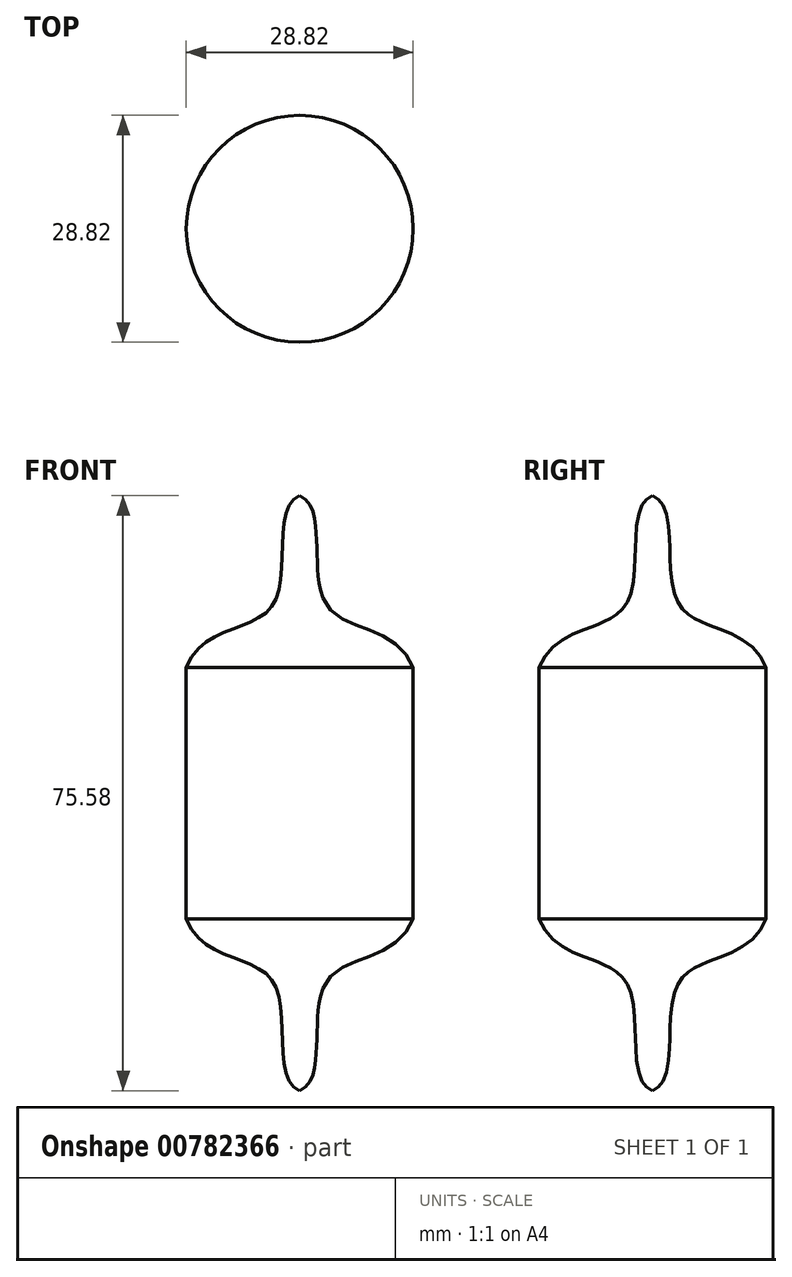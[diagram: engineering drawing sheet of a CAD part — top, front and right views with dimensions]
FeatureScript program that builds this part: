
annotation { "Feature Type Name" : "Feature", "Feature Type Description" : "" }
export const myFeature = defineFeature(function(context is Context, id is Id, definition is map)
    precondition{}
    {
        {
            var Q0;
            Q0=qCreatedBy(makeId("Front.planeOp"),FACE);
            var sketch = newSketch(context, id + "F0", { "sketchPlane" : qUnion([Q0])});
            skLineSegment(sketch, "E0", {"start": v(-14.41, 0) * mm, "end": v(-14.41, 16) * mm});
            skLineSegment(sketch, "E1.MirrorCS", {"start": v(-14.41, 0) * mm, "end": v(-14.41, -16) * mm});
            skFitSpline(sketch, "E2", {"points": [v(-14.41, 16) * mm, v(-3.3, 24.1) * mm, v(0, 37.8) * mm], "startDerivative": vector(13.65, 33.4) * mm, "endDerivative": vector(21.2, 7.86) * mm});
            skFitSpline(sketch, "E3.MirrorCS", {"points": [v(-14.41, -16) * mm, v(-3.3, -24.1) * mm, v(0, -37.8) * mm], "startDerivative": vector(13.65, -33.4) * mm, "endDerivative": vector(21.2, -7.86) * mm});
            skLineSegment(sketch, "E4", {"start": v(0, 37.8) * mm, "end": v(0, -37.8) * mm});
            skSolve(sketch);
        }
        {
            var Q0;
            Q0 = qSketchRegion(id + "F0", true);
            var Q1;
            Q1=sQuery(id+"F0.wireOp",EDGE,"E4");
            revolve(context, id + "F1", {"surfaceOperationType" : NewSurfaceOperationType.NEW, "entities" : qUnion([Q0]), "axis" : qUnion([Q1]), "revolveType" : RevolveType.FULL});
        }
    });
